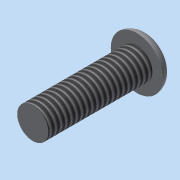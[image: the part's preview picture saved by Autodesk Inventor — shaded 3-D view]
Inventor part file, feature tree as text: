
AUTODESK INVENTOR PART (.ipt)
format: ipt  version: 2015 (Build 190159000, 159)  size: 98,304 bytes
history: native  units: mm
features: revolve x1, fillet x1, thread x1, sketch x1
ambient origin geometry x8: Origin, YZ Plane, XZ Plane, XY Plane, X Axis, Y Axis, Z Axis, Center Point
bodies: Solid1 (feature_tree)
feature tree (4):
  revolve  "Revolution1"  [1 undecoded]
  fillet  "Fillet1"  Radius=1.0mm
  thread  "Thread1"  [1 undecoded]
  sketch  "Sketch1"  dims[d0=1.5mm d1=2.5mm d2=1.0mm d3=90.0deg d4=1.0mm d5=10.0mm d6=0.0mm d7=10.0mm]
note: 2 required parameter values undecoded (feature->parameter linkage not recoverable at this tier; creation-order binding heuristic only, values carry confidence <= 0.55)